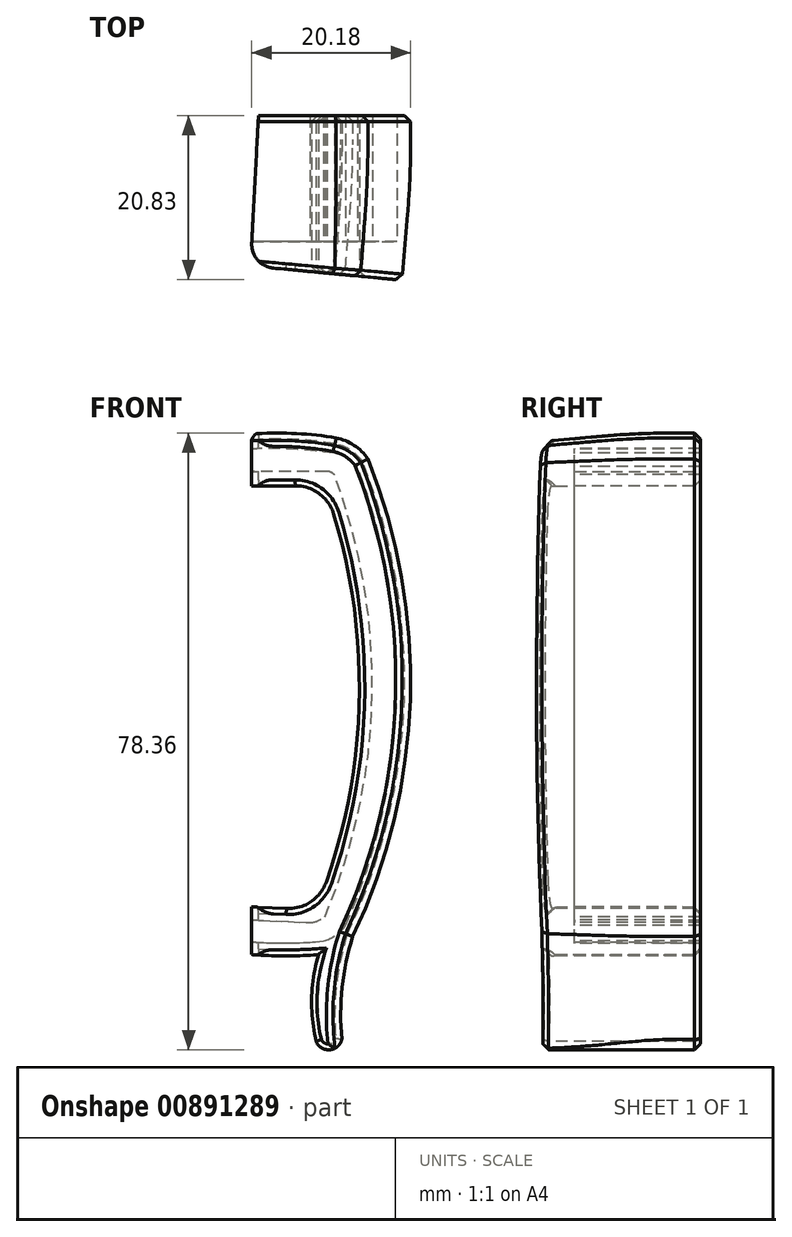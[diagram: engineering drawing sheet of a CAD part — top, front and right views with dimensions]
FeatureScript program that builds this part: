
annotation { "Feature Type Name" : "Feature", "Feature Type Description" : "" }
export const myFeature = defineFeature(function(context is Context, id is Id, definition is map)
    precondition{}
    {
        {
            var Q0;
            Q0=qCreatedBy(makeId("Front.planeOp"),FACE);
            var sketch = newSketch(context, id + "F0", { "sketchPlane" : qUnion([Q0])});
            skArc(sketch, "E0", {"start": v(-38.9, -29.21) * mm, "mid": v(-32.41, -0.21) * mm, "end": v(-37.38, 29.09) * mm});
            skArc(sketch, "E1", {"start": v(-41.54, -28.08) * mm, "mid": v(-35.53, -0.12) * mm, "end": v(-40.34, 28.07) * mm});
            skArc(sketch, "E2", {"start": v(-37.38, 29.09) * mm, "mid": v(-38.7, 30.21) * mm, "end": v(-40.34, 30.8) * mm});
            skArc(sketch, "E3", {"start": v(-41.68, -31.17) * mm, "mid": v(-40.13, -30.41) * mm, "end": v(-38.9, -29.21) * mm});
            skArc(sketch, "E4", {"start": v(-43.45, -28.83) * mm, "mid": v(-42.44, -28.6) * mm, "end": v(-41.54, -28.08) * mm});
            skArc(sketch, "E5", {"start": v(-40.34, 28.07) * mm, "mid": v(-40.75, 28.38) * mm, "end": v(-41.26, 28.5) * mm});
            skLineSegment(sketch, "E6", {"start": v(-41.26, 28.5) * mm, "end": v(-50.85, 28.5) * mm});
            skArc(sketch, "E7", {"start": v(-40.34, 30.8) * mm, "mid": v(-45.58, 31.33) * mm, "end": v(-50.85, 31.34) * mm});
            skArc(sketch, "E8", {"start": v(-50.85, -31.27) * mm, "mid": v(-46.27, -31.43) * mm, "end": v(-41.68, -31.17) * mm});
            skLineSegment(sketch, "E9", {"start": v(-50.85, -28.49) * mm, "end": v(-43.45, -28.83) * mm});
            skLineSegment(sketch, "E10", {"start": v(-50.85, 31.34) * mm, "end": v(-50.85, 33.24) * mm});
            skLineSegment(sketch, "E11", {"start": v(-50.85, 28.5) * mm, "end": v(-50.85, 26.66) * mm});
            skArc(sketch, "E12", {"start": v(-40.1, 32.76) * mm, "mid": v(-45.46, 33.32) * mm, "end": v(-50.85, 33.24) * mm});
            skArc(sketch, "E13", {"start": v(-36.07, 30.09) * mm, "mid": v(-37.83, 31.8) * mm, "end": v(-40.1, 32.76) * mm});
            skArc(sketch, "E14", {"start": v(-38, -30.6) * mm, "mid": v(-30.69, -0.46) * mm, "end": v(-36.07, 30.09) * mm});
            skArc(sketch, "E15", {"start": v(-50.85, -32.89) * mm, "mid": v(-46.15, -33.05) * mm, "end": v(-41.45, -32.84) * mm});
            skArc(sketch, "E16", {"start": v(-41.45, -32.84) * mm, "mid": v(-39.6, -31.9) * mm, "end": v(-38, -30.6) * mm});
            skLineSegment(sketch, "E17", {"start": v(-50.85, -31.27) * mm, "end": v(-50.85, -32.89) * mm});
            skLineSegment(sketch, "E18", {"start": v(-50.85, -28.49) * mm, "end": v(-50.85, -26.83) * mm});
            skLineSegment(sketch, "E19", {"start": v(-50.85, -26.83) * mm, "end": v(-43.45, -27.17) * mm});
            skArc(sketch, "E20", {"start": v(-42.57, -26.88) * mm, "mid": v(-37.16, -0.2) * mm, "end": v(-41.61, 26.66) * mm});
            skArc(sketch, "E21", {"start": v(-43.45, -27.17) * mm, "mid": v(-42.98, -27.1) * mm, "end": v(-42.57, -26.88) * mm});
            skLineSegment(sketch, "E22", {"start": v(-50.85, 26.66) * mm, "end": v(-41.61, 26.66) * mm});
            skLineSegment(sketch, "E23", {"start": v(-50.85, 31.34) * mm, "end": v(-50.85, 28.5) * mm});
            skLineSegment(sketch, "E24", {"start": v(-50.85, -28.49) * mm, "end": v(-50.85, -31.27) * mm});
            skArc(sketch, "E25", {"start": v(-38, -30.6) * mm, "mid": v(-39.34, -37.06) * mm, "end": v(-39.39, -43.66) * mm});
            skArc(sketch, "E26", {"start": v(-42.34, -32.9) * mm, "mid": v(-43.22, -38.4) * mm, "end": v(-42.65, -43.93) * mm});
            skArc(sketch, "E27", {"start": v(-42.65, -43.93) * mm, "mid": v(-40.92, -45) * mm, "end": v(-39.39, -43.66) * mm});
            skSolve(sketch);
        }
        {
            var Q0;
            Q0=makeQuery(id+"F0.imprint","IMPRINT",FACE,{"disambiguationData":[TD([[makeQuery(id+"F0.imprint","IMPRINT",EDGE,{"derivedFrom":sQuery(id+"F0.wireOp",EDGE,"E1")}),1.0]])]});
            var Q1;
            Q1=makeQuery(id+"F0.imprint","IMPRINT",FACE,{"disambiguationData":[TD([[makeQuery(id+"F0.imprint","IMPRINT",EDGE,{"derivedFrom":sQuery(id+"F0.wireOp",EDGE,"E0")}),-1.0]])]});
            var Q2;
            {var subQ1=sQuery(id+"F0.wireOp",EDGE,"E16");Q2=makeQuery(id+"F0.imprint","IMPRINT",FACE,{"disambiguationData":[TD([[makeQuery(id+"F0.imprint","IMPRINT",EDGE,{"derivedFrom":subQ1}),-1.0]])]});}
            extrude(context, id + "F1", {"entities" : qUnion([Q0, Q1, Q2]), "oppositeDirection" : true, "depth" : 20.07 * mm, "offsetDistance" : 25.4 * mm});
        }
        {
            var Q0;
            Q0=makeQuery(id+"F0.imprint","IMPRINT",FACE,{"disambiguationData":[TD([[makeQuery(id+"F0.imprint","IMPRINT",EDGE,{"derivedFrom":sQuery(id+"F0.wireOp",EDGE,"E0")}),1.0]])]});
            extrude(context, id + "F2", {"entities" : qUnion([Q0]), "oppositeDirection" : true, "depth" : 4.06 * mm, "offsetDistance" : 25.4 * mm});
        }
        {
            var Q0;
            Q0=makeQuery(id+"F2.opExtrude","SWEPT_BODY",BODY,{"disambiguationData":[OSD([sQuery(id+"F0.wireOp",EDGE,"E0"),sQuery(id+"F0.wireOp",EDGE,"E1"),sQuery(id+"F0.wireOp",EDGE,"E2"),sQuery(id+"F0.wireOp",EDGE,"E3"),sQuery(id+"F0.wireOp",EDGE,"E4"),sQuery(id+"F0.wireOp",EDGE,"E5"),sQuery(id+"F0.wireOp",EDGE,"E6"),sQuery(id+"F0.wireOp",EDGE,"E7"),sQuery(id+"F0.wireOp",EDGE,"E8"),sQuery(id+"F0.wireOp",EDGE,"E9"),sQuery(id+"F0.wireOp",EDGE,"E23"),sQuery(id+"F0.wireOp",EDGE,"E24")])]});
            var Q1;
            Q1=makeQuery(id+"F1.opExtrude","SWEPT_BODY",BODY,{"disambiguationData":[OSD([sQuery(id+"F0.wireOp",EDGE,"E1"),sQuery(id+"F0.wireOp",EDGE,"E4"),sQuery(id+"F0.wireOp",EDGE,"E5"),sQuery(id+"F0.wireOp",EDGE,"E6"),sQuery(id+"F0.wireOp",EDGE,"E9"),sQuery(id+"F0.wireOp",EDGE,"E11"),sQuery(id+"F0.wireOp",EDGE,"E18"),sQuery(id+"F0.wireOp",EDGE,"E19"),sQuery(id+"F0.wireOp",EDGE,"E20"),sQuery(id+"F0.wireOp",EDGE,"E21"),sQuery(id+"F0.wireOp",EDGE,"E22")])]});
            var Q2;
            Q2=makeQuery(id+"F1.opExtrude","SWEPT_BODY",BODY,{"disambiguationData":[OSD([sQuery(id+"F0.wireOp",EDGE,"E0"),sQuery(id+"F0.wireOp",EDGE,"E2"),sQuery(id+"F0.wireOp",EDGE,"E3"),sQuery(id+"F0.wireOp",EDGE,"E7"),sQuery(id+"F0.wireOp",EDGE,"E8"),sQuery(id+"F0.wireOp",EDGE,"E10"),sQuery(id+"F0.wireOp",EDGE,"E12"),sQuery(id+"F0.wireOp",EDGE,"E13"),sQuery(id+"F0.wireOp",EDGE,"E14"),sQuery(id+"F0.wireOp",EDGE,"E15"),sQuery(id+"F0.wireOp",EDGE,"E16"),sQuery(id+"F0.wireOp",EDGE,"E17")])]});
            booleanBodies(context, id + "F3", {"operationType" : BooleanOperationType.UNION, "tools" : qUnion([Q0, Q1, Q2])});
        }
        {
            var Q0;
            {var subQ0=sQuery(id+"F0.wireOp",EDGE,"E9");var subQ1=sQuery(id+"F0.wireOp",EDGE,"E8");var subQ2=sQuery(id+"F0.wireOp",EDGE,"E7");var subQ3=sQuery(id+"F0.wireOp",EDGE,"E6");var subQ4=sQuery(id+"F0.wireOp",EDGE,"E5");var subQ5=sQuery(id+"F0.wireOp",EDGE,"E4");var subQ6=sQuery(id+"F0.wireOp",EDGE,"E3");var subQ7=sQuery(id+"F0.wireOp",EDGE,"E2");var subQ8=sQuery(id+"F0.wireOp",EDGE,"E1");var subQ9=sQuery(id+"F0.wireOp",EDGE,"E0");Q0=makeQuery(id+"F3.opBoolean","MERGE",FACE,{"derivedFrom":[makeQuery(id+"F1.opExtrude","CAP_FACE",FACE,{"disambiguationData":[OSD([subQ9,subQ7,subQ6,subQ2,subQ1,sQuery(id+"F0.wireOp",EDGE,"E10"),sQuery(id+"F0.wireOp",EDGE,"E12"),sQuery(id+"F0.wireOp",EDGE,"E13"),sQuery(id+"F0.wireOp",EDGE,"E14"),sQuery(id+"F0.wireOp",EDGE,"E15"),sQuery(id+"F0.wireOp",EDGE,"E17"),sQuery(id+"F0.wireOp",EDGE,"E25"),sQuery(id+"F0.wireOp",EDGE,"E26"),sQuery(id+"F0.wireOp",EDGE,"E27")])],"isStart":true}),makeQuery(id+"F1.opExtrude","CAP_FACE",FACE,{"disambiguationData":[OSD([subQ8,subQ5,subQ4,subQ3,subQ0,sQuery(id+"F0.wireOp",EDGE,"E11"),sQuery(id+"F0.wireOp",EDGE,"E18"),sQuery(id+"F0.wireOp",EDGE,"E19"),sQuery(id+"F0.wireOp",EDGE,"E20"),sQuery(id+"F0.wireOp",EDGE,"E21"),sQuery(id+"F0.wireOp",EDGE,"E22")])],"isStart":true}),makeQuery(id+"F2.opExtrude","CAP_FACE",FACE,{"disambiguationData":[OSD([subQ9,subQ8,subQ7,subQ6,subQ5,subQ4,subQ3,subQ2,subQ1,subQ0,sQuery(id+"F0.wireOp",EDGE,"E23"),sQuery(id+"F0.wireOp",EDGE,"E24")])],"isStart":true})]});}
            extrude(context, id + "F4", {"entities" : qUnion([Q0]), "operationType" : NewBodyOperationType.ADD, "depth" : 2.54 * mm, "offsetDistance" : 25.4 * mm});
        }
        {
            var Q0;
            Q0=makeQuery(id+"F4.opExtrude","CAP_EDGE",EDGE,{"disambiguationData":[OSD([sQuery(id+"F0.wireOp",EDGE,"E14")])],"isStart":false});
            var Q1;
            Q1=makeQuery(id+"F4.opExtrude","CAP_EDGE",EDGE,{"disambiguationData":[OSD([sQuery(id+"F0.wireOp",EDGE,"E12")])],"isStart":false});
            var Q2;
            Q2=makeQuery(id+"F4.opExtrude","CAP_EDGE",EDGE,{"disambiguationData":[OSD([sQuery(id+"F0.wireOp",EDGE,"E13")])],"isStart":false});
            var Q3;
            Q3=makeQuery(id+"F4.opExtrude","CAP_EDGE",EDGE,{"disambiguationData":[OSD([sQuery(id+"F0.wireOp",EDGE,"E25")])],"isStart":false});
            chamfer(context, id + "F5", {"entities" : qUnion([Q0, Q1, Q2, Q3]), "chamferType" : ChamferType.OFFSET_ANGLE, "width" : 1.27 * mm, "oppositeDirection" : false, "angle" : 85 * degree, "tangentPropagation" : true});
        }
        {
            var Q0;
            {var subQ0=sQuery(id+"F0.wireOp",EDGE,"E14");Q0=makeQuery(id+"F5.opChamfer","BLEND_EDGE",EDGE,{"blendedFrom":[makeQuery(id+"F4.opExtrude","CAP_EDGE",EDGE,{"disambiguationData":[OSD([subQ0])],"isStart":false}),makeQuery(id+"F4.boolean.opBoolean","MERGE",FACE,{"derivedFrom":[makeQuery(id+"F1.opExtrude","SWEPT_FACE",FACE,{"disambiguationData":[OSD([subQ0])]}),makeQuery(id+"F4.opExtrude","SWEPT_FACE",FACE,{"disambiguationData":[OSD([subQ0])]})]})],"blendedInto":[makeQuery(id+"F4.boolean.opBoolean","MERGE",FACE,{"derivedFrom":[makeQuery(id+"F1.opExtrude","SWEPT_FACE",FACE,{"disambiguationData":[OSD([subQ0])]}),makeQuery(id+"F4.opExtrude","SWEPT_FACE",FACE,{"disambiguationData":[OSD([subQ0])]})]})]});}
            var Q1;
            {var subQ0=sQuery(id+"F0.wireOp",EDGE,"E13");Q1=makeQuery(id+"F5.opChamfer","BLEND_EDGE",EDGE,{"blendedFrom":[makeQuery(id+"F4.opExtrude","CAP_EDGE",EDGE,{"disambiguationData":[OSD([subQ0])],"isStart":false}),makeQuery(id+"F4.boolean.opBoolean","MERGE",FACE,{"derivedFrom":[makeQuery(id+"F1.opExtrude","SWEPT_FACE",FACE,{"disambiguationData":[OSD([subQ0])]}),makeQuery(id+"F4.opExtrude","SWEPT_FACE",FACE,{"disambiguationData":[OSD([subQ0])]})]})],"blendedInto":[makeQuery(id+"F4.boolean.opBoolean","MERGE",FACE,{"derivedFrom":[makeQuery(id+"F1.opExtrude","SWEPT_FACE",FACE,{"disambiguationData":[OSD([subQ0])]}),makeQuery(id+"F4.opExtrude","SWEPT_FACE",FACE,{"disambiguationData":[OSD([subQ0])]})]})]});}
            var Q2;
            {var subQ0=sQuery(id+"F0.wireOp",EDGE,"E12");Q2=makeQuery(id+"F5.opChamfer","BLEND_EDGE",EDGE,{"blendedFrom":[makeQuery(id+"F4.opExtrude","CAP_EDGE",EDGE,{"disambiguationData":[OSD([subQ0])],"isStart":false}),makeQuery(id+"F4.boolean.opBoolean","MERGE",FACE,{"derivedFrom":[makeQuery(id+"F1.opExtrude","SWEPT_FACE",FACE,{"disambiguationData":[OSD([subQ0])]}),makeQuery(id+"F4.opExtrude","SWEPT_FACE",FACE,{"disambiguationData":[OSD([subQ0])]})]})],"blendedInto":[makeQuery(id+"F4.boolean.opBoolean","MERGE",FACE,{"derivedFrom":[makeQuery(id+"F1.opExtrude","SWEPT_FACE",FACE,{"disambiguationData":[OSD([subQ0])]}),makeQuery(id+"F4.opExtrude","SWEPT_FACE",FACE,{"disambiguationData":[OSD([subQ0])]})]})]});}
            var Q3;
            {var subQ0=sQuery(id+"F0.wireOp",EDGE,"E25");Q3=makeQuery(id+"F5.opChamfer","BLEND_EDGE",EDGE,{"blendedFrom":[makeQuery(id+"F4.opExtrude","CAP_EDGE",EDGE,{"disambiguationData":[OSD([subQ0])],"isStart":false}),makeQuery(id+"F4.boolean.opBoolean","MERGE",FACE,{"derivedFrom":[makeQuery(id+"F1.opExtrude","SWEPT_FACE",FACE,{"disambiguationData":[OSD([subQ0])]}),makeQuery(id+"F4.opExtrude","SWEPT_FACE",FACE,{"disambiguationData":[OSD([subQ0])]})]})],"blendedInto":[makeQuery(id+"F4.boolean.opBoolean","MERGE",FACE,{"derivedFrom":[makeQuery(id+"F1.opExtrude","SWEPT_FACE",FACE,{"disambiguationData":[OSD([subQ0])]}),makeQuery(id+"F4.opExtrude","SWEPT_FACE",FACE,{"disambiguationData":[OSD([subQ0])]})]})]});}
            fillet(context, id + "F6", {"entities" : qUnion([Q0, Q1, Q2, Q3]), "radius" : 101.6 * mm, "tangentPropagation" : true, "allowEdgeOverflow" : false});
        }
        {
            var Q0;
            Q0=qCreatedBy(makeId("Top.planeOp"),FACE);
            cPlane(context, id + "F7", {"entities" : qUnion([Q0]), "cplaneType" : CPlaneType.OFFSET, "offset" : 33.78 * mm, "width" : 152.4 * mm, "height" : 152.4 * mm});
        }
        {
            var Q0;
            Q0=qCreatedBy(id+"F7.planeOp",FACE);
            var sketch = newSketch(context, id + "F8", { "sketchPlane" : qUnion([Q0])});
            skLineSegment(sketch, "E28", {"start": v(-26.85, -1.3) * mm, "end": v(-60.38, 1.86) * mm});
            skLineSegment(sketch, "E29", {"start": v(-26.85, -1.3) * mm, "end": v(-51.2, -11.53) * mm});
            skLineSegment(sketch, "E30", {"start": v(-51.2, -11.53) * mm, "end": v(-60.38, 1.86) * mm});
            skLineSegment(sketch, "E31", {"start": v(-50.07, 25.3) * mm, "end": v(-58.4, 26.09) * mm});
            skLineSegment(sketch, "E32", {"start": v(-58.4, 26.09) * mm, "end": v(-60.38, 1.86) * mm});
            skLineSegment(sketch, "E33", {"start": v(-50.98, 0.97) * mm, "end": v(-49.82, 22.9) * mm});
            skLineSegment(sketch, "E34", {"start": v(-49.82, 22.9) * mm, "end": v(-50.07, 25.3) * mm});
            skSolve(sketch);
        }
        {
            var Q0;
            Q0=makeQuery(id+"F8.imprint","IMPRINT",FACE,{"disambiguationData":[TD([[makeQuery(id+"F8.imprint","IMPRINT",EDGE,{"derivedFrom":sQuery(id+"F8.wireOp",EDGE,"E28")}),1.0]])]});
            var Q1;
            {var subQ2=sQuery(id+"F8.wireOp",EDGE,"ddrIeZ3n-C3nf-GXhr-pW9J-iitOHfDZmZ50");Q1=makeQuery(id+"F8.imprint","IMPRINT",FACE,{"disambiguationData":[TD([[makeQuery(id+"F8.imprint","IMPRINT",EDGE,{"derivedFrom":subQ2}),1.0]])]});}
            var Q2;
            Q2=makeQuery(id+"F8.imprint","IMPRINT",FACE,{"disambiguationData":[TD([[makeQuery(id+"F8.imprint","IMPRINT",EDGE,{"derivedFrom":sQuery(id+"F8.wireOp",EDGE,"E31")}),1.0]])]});
            extrude(context, id + "F9", {"entities" : qUnion([Q0, Q1, Q2]), "operationType" : NewBodyOperationType.REMOVE, "oppositeDirection" : true, "depth" : 254 * mm, "offsetDistance" : 25.4 * mm});
        }
        {
            var Q0;
            {var subQ0=sQuery(id+"F0.wireOp",EDGE,"E22");var subQ1=sQuery(id+"F0.wireOp",EDGE,"E20");Q0=makeQuery(id+"F4.boolean.opBoolean","MERGE",EDGE,{"derivedFrom":[makeQuery(id+"F1.opExtrude","SWEPT_EDGE",EDGE,{"disambiguationData":[OSD([subQ1,subQ0])]}),makeQuery(id+"F4.opExtrude","SWEPT_EDGE",EDGE,{"disambiguationData":[OSD([subQ1,subQ0])]})]});}
            var Q1;
            {var subQ0=sQuery(id+"F0.wireOp",EDGE,"E21");var subQ1=sQuery(id+"F0.wireOp",EDGE,"E20");Q1=makeQuery(id+"F4.boolean.opBoolean","MERGE",EDGE,{"derivedFrom":[makeQuery(id+"F1.opExtrude","SWEPT_EDGE",EDGE,{"disambiguationData":[OSD([subQ1,subQ0])]}),makeQuery(id+"F4.opExtrude","SWEPT_EDGE",EDGE,{"disambiguationData":[OSD([subQ1,subQ0])]})]});}
            fillet(context, id + "F10", {"entities" : qUnion([Q0, Q1]), "radius" : 5.08 * mm, "tangentPropagation" : true, "allowEdgeOverflow" : false});
        }
        {
            var Q0;
            Q0=makeQuery(id+"F9.boolean.opBoolean","INTERSECT",EDGE,{"derivedFrom":[makeQuery(id+"F5.opChamfer","BLEND_FACE",FACE,{"disambiguationData":[OSD([sQuery(id+"F0.wireOp",EDGE,"E14")])]}),makeQuery(id+"F9.opExtrude","SWEPT_FACE",FACE,{"disambiguationData":[OSD([sQuery(id+"F8.wireOp",EDGE,"E28")])]})]});
            var Q1;
            Q1=makeQuery(id+"F9.boolean.opBoolean","INTERSECT",EDGE,{"derivedFrom":[makeQuery(id+"F5.opChamfer","BLEND_FACE",FACE,{"disambiguationData":[OSD([sQuery(id+"F0.wireOp",EDGE,"E13")])]}),makeQuery(id+"F9.opExtrude","SWEPT_FACE",FACE,{"disambiguationData":[OSD([sQuery(id+"F8.wireOp",EDGE,"E28")])]})]});
            var Q2;
            Q2=makeQuery(id+"F9.boolean.opBoolean","INTERSECT",EDGE,{"derivedFrom":[makeQuery(id+"F5.opChamfer","BLEND_FACE",FACE,{"disambiguationData":[OSD([sQuery(id+"F0.wireOp",EDGE,"E12")])]}),makeQuery(id+"F9.opExtrude","SWEPT_FACE",FACE,{"disambiguationData":[OSD([sQuery(id+"F8.wireOp",EDGE,"E28")])]})]});
            var Q3;
            Q3=makeQuery(id+"F9.boolean.opBoolean","INTERSECT",EDGE,{"derivedFrom":[makeQuery(id+"F5.opChamfer","BLEND_FACE",FACE,{"disambiguationData":[OSD([sQuery(id+"F0.wireOp",EDGE,"E25")])]}),makeQuery(id+"F9.opExtrude","SWEPT_FACE",FACE,{"disambiguationData":[OSD([sQuery(id+"F8.wireOp",EDGE,"E28")])]})]});
            var Q4;
            {var subQ0=sQuery(id+"F0.wireOp",EDGE,"E26");Q4=makeQuery(id+"F9.boolean.opBoolean","INTERSECT",EDGE,{"derivedFrom":[makeQuery(id+"F4.boolean.opBoolean","MERGE",FACE,{"derivedFrom":[makeQuery(id+"F1.opExtrude","SWEPT_FACE",FACE,{"disambiguationData":[OSD([subQ0])]}),makeQuery(id+"F4.opExtrude","SWEPT_FACE",FACE,{"disambiguationData":[OSD([subQ0])]})]}),makeQuery(id+"F9.opExtrude","SWEPT_FACE",FACE,{"disambiguationData":[OSD([sQuery(id+"F8.wireOp",EDGE,"E28")])]})]});}
            var Q5;
            {var subQ0=sQuery(id+"F0.wireOp",EDGE,"E27");Q5=makeQuery(id+"F9.boolean.opBoolean","INTERSECT",EDGE,{"derivedFrom":[makeQuery(id+"F4.boolean.opBoolean","MERGE",FACE,{"derivedFrom":[makeQuery(id+"F1.opExtrude","SWEPT_FACE",FACE,{"disambiguationData":[OSD([subQ0])]}),makeQuery(id+"F4.opExtrude","SWEPT_FACE",FACE,{"disambiguationData":[OSD([subQ0])]})]}),makeQuery(id+"F9.opExtrude","SWEPT_FACE",FACE,{"disambiguationData":[OSD([sQuery(id+"F8.wireOp",EDGE,"E28")])]})]});}
            var Q6;
            {var subQ0=sQuery(id+"F0.wireOp",EDGE,"E15");Q6=makeQuery(id+"F9.boolean.opBoolean","INTERSECT",EDGE,{"derivedFrom":[makeQuery(id+"F4.boolean.opBoolean","MERGE",FACE,{"derivedFrom":[makeQuery(id+"F1.opExtrude","SWEPT_FACE",FACE,{"disambiguationData":[OSD([subQ0])]}),makeQuery(id+"F4.opExtrude","SWEPT_FACE",FACE,{"disambiguationData":[OSD([subQ0])]})]}),makeQuery(id+"F9.opExtrude","SWEPT_FACE",FACE,{"disambiguationData":[OSD([sQuery(id+"F8.wireOp",EDGE,"E28")])]})]});}
            var Q7;
            {var subQ0=sQuery(id+"F0.wireOp",EDGE,"E21");var subQ1=sQuery(id+"F0.wireOp",EDGE,"E20");Q7=makeQuery(id+"F10.opFillet","BLEND_EDGE",EDGE,{"blendedFrom":[makeQuery(id+"F4.boolean.opBoolean","MERGE",EDGE,{"derivedFrom":[makeQuery(id+"F1.opExtrude","SWEPT_EDGE",EDGE,{"disambiguationData":[OSD([subQ1,subQ0])]}),makeQuery(id+"F4.opExtrude","SWEPT_EDGE",EDGE,{"disambiguationData":[OSD([subQ1,subQ0])]})]}),makeQuery(id+"F9.boolean.opBoolean","COPY",FACE,{"derivedFrom":makeQuery(id+"F9.opExtrude","SWEPT_FACE",FACE,{"disambiguationData":[OSD([sQuery(id+"F8.wireOp",EDGE,"E28")])]})})],"blendedInto":[makeQuery(id+"F9.boolean.opBoolean","COPY",FACE,{"derivedFrom":makeQuery(id+"F9.opExtrude","SWEPT_FACE",FACE,{"disambiguationData":[OSD([sQuery(id+"F8.wireOp",EDGE,"E28")])]})})]});}
            var Q8;
            {var subQ0=sQuery(id+"F0.wireOp",EDGE,"E20");Q8=makeQuery(id+"F9.boolean.opBoolean","INTERSECT",EDGE,{"derivedFrom":[makeQuery(id+"F4.boolean.opBoolean","MERGE",FACE,{"derivedFrom":[makeQuery(id+"F1.opExtrude","SWEPT_FACE",FACE,{"disambiguationData":[OSD([subQ0])]}),makeQuery(id+"F4.opExtrude","SWEPT_FACE",FACE,{"disambiguationData":[OSD([subQ0])]})]}),makeQuery(id+"F9.opExtrude","SWEPT_FACE",FACE,{"disambiguationData":[OSD([sQuery(id+"F8.wireOp",EDGE,"E28")])]})]});}
            var Q9;
            {var subQ0=sQuery(id+"F0.wireOp",EDGE,"E19");Q9=makeQuery(id+"F9.boolean.opBoolean","INTERSECT",EDGE,{"derivedFrom":[makeQuery(id+"F4.boolean.opBoolean","MERGE",FACE,{"derivedFrom":[makeQuery(id+"F1.opExtrude","SWEPT_FACE",FACE,{"disambiguationData":[OSD([subQ0])]}),makeQuery(id+"F4.opExtrude","SWEPT_FACE",FACE,{"disambiguationData":[OSD([subQ0])]})]}),makeQuery(id+"F9.opExtrude","SWEPT_FACE",FACE,{"disambiguationData":[OSD([sQuery(id+"F8.wireOp",EDGE,"E28")])]})]});}
            var Q10;
            {var subQ0=sQuery(id+"F0.wireOp",EDGE,"E22");var subQ1=sQuery(id+"F0.wireOp",EDGE,"E20");Q10=makeQuery(id+"F10.opFillet","BLEND_EDGE",EDGE,{"blendedFrom":[makeQuery(id+"F4.boolean.opBoolean","MERGE",EDGE,{"derivedFrom":[makeQuery(id+"F1.opExtrude","SWEPT_EDGE",EDGE,{"disambiguationData":[OSD([subQ1,subQ0])]}),makeQuery(id+"F4.opExtrude","SWEPT_EDGE",EDGE,{"disambiguationData":[OSD([subQ1,subQ0])]})]}),makeQuery(id+"F9.boolean.opBoolean","COPY",FACE,{"derivedFrom":makeQuery(id+"F9.opExtrude","SWEPT_FACE",FACE,{"disambiguationData":[OSD([sQuery(id+"F8.wireOp",EDGE,"E28")])]})})],"blendedInto":[makeQuery(id+"F9.boolean.opBoolean","COPY",FACE,{"derivedFrom":makeQuery(id+"F9.opExtrude","SWEPT_FACE",FACE,{"disambiguationData":[OSD([sQuery(id+"F8.wireOp",EDGE,"E28")])]})})]});}
            var Q11;
            {var subQ0=sQuery(id+"F0.wireOp",EDGE,"E22");Q11=makeQuery(id+"F9.boolean.opBoolean","INTERSECT",EDGE,{"derivedFrom":[makeQuery(id+"F4.boolean.opBoolean","MERGE",FACE,{"derivedFrom":[makeQuery(id+"F1.opExtrude","SWEPT_FACE",FACE,{"disambiguationData":[OSD([subQ0])]}),makeQuery(id+"F4.opExtrude","SWEPT_FACE",FACE,{"disambiguationData":[OSD([subQ0])]})]}),makeQuery(id+"F9.opExtrude","SWEPT_FACE",FACE,{"disambiguationData":[OSD([sQuery(id+"F8.wireOp",EDGE,"E28")])]})]});}
            var Q12;
            Q12=makeQuery(id+"F1.opExtrude","CAP_EDGE",EDGE,{"disambiguationData":[OSD([sQuery(id+"F0.wireOp",EDGE,"E20")])],"isStart":false});
            var Q13;
            Q13=makeQuery(id+"F1.opExtrude","CAP_EDGE",EDGE,{"disambiguationData":[OSD([sQuery(id+"F0.wireOp",EDGE,"E14")])],"isStart":false});
            var Q14;
            Q14=makeQuery(id+"F1.opExtrude","CAP_EDGE",EDGE,{"disambiguationData":[OSD([sQuery(id+"F0.wireOp",EDGE,"E13")])],"isStart":false});
            var Q15;
            Q15=makeQuery(id+"F1.opExtrude","CAP_EDGE",EDGE,{"disambiguationData":[OSD([sQuery(id+"F0.wireOp",EDGE,"E12")])],"isStart":false});
            var Q16;
            Q16=makeQuery(id+"F1.opExtrude","CAP_EDGE",EDGE,{"disambiguationData":[OSD([sQuery(id+"F0.wireOp",EDGE,"E25")])],"isStart":false});
            var Q17;
            Q17=makeQuery(id+"F1.opExtrude","CAP_EDGE",EDGE,{"disambiguationData":[OSD([sQuery(id+"F0.wireOp",EDGE,"E26")])],"isStart":false});
            var Q18;
            Q18=makeQuery(id+"F1.opExtrude","CAP_EDGE",EDGE,{"disambiguationData":[OSD([sQuery(id+"F0.wireOp",EDGE,"E27")])],"isStart":false});
            var Q19;
            Q19=makeQuery(id+"F1.opExtrude","CAP_EDGE",EDGE,{"disambiguationData":[OSD([sQuery(id+"F0.wireOp",EDGE,"E15")])],"isStart":false});
            chamfer(context, id + "F11", {"entities" : qUnion([Q0, Q1, Q2, Q3, Q4, Q5, Q6, Q7, Q8, Q9, Q10, Q11, Q12, Q13, Q14, Q15, Q16, Q17, Q18, Q19]), "width" : 0.76 * mm, "tangentPropagation" : true});
        }
        {
            var Q0;
            {var subQ0=sQuery(id+"F0.wireOp",EDGE,"E23");var subQ1=sQuery(id+"F0.wireOp",EDGE,"E11");var subQ2=sQuery(id+"F0.wireOp",EDGE,"E10");Q0=makeQuery(id+"F9.boolean.opBoolean","INTERSECT",EDGE,{"derivedFrom":[makeQuery(id+"F4.boolean.opBoolean","MERGE",FACE,{"derivedFrom":[makeQuery(id+"F3.opBoolean","MERGE",FACE,{"derivedFrom":[makeQuery(id+"F1.opExtrude","SWEPT_FACE",FACE,{"disambiguationData":[OSD([subQ2])]}),makeQuery(id+"F1.opExtrude","SWEPT_FACE",FACE,{"disambiguationData":[OSD([subQ1])]}),makeQuery(id+"F2.opExtrude","SWEPT_FACE",FACE,{"disambiguationData":[OSD([subQ0])]})]}),makeQuery(id+"F4.opExtrude","SWEPT_FACE",FACE,{"disambiguationData":[OSD([subQ2,subQ1,subQ0])]})]}),makeQuery(id+"F9.opExtrude","SWEPT_FACE",FACE,{"disambiguationData":[OSD([sQuery(id+"F8.wireOp",EDGE,"E28")])]})]});}
            var Q1;
            {var subQ0=sQuery(id+"F0.wireOp",EDGE,"E24");var subQ1=sQuery(id+"F0.wireOp",EDGE,"E18");var subQ2=sQuery(id+"F0.wireOp",EDGE,"E17");Q1=makeQuery(id+"F9.boolean.opBoolean","INTERSECT",EDGE,{"derivedFrom":[makeQuery(id+"F4.boolean.opBoolean","MERGE",FACE,{"derivedFrom":[makeQuery(id+"F3.opBoolean","MERGE",FACE,{"derivedFrom":[makeQuery(id+"F1.opExtrude","SWEPT_FACE",FACE,{"disambiguationData":[OSD([subQ2])]}),makeQuery(id+"F1.opExtrude","SWEPT_FACE",FACE,{"disambiguationData":[OSD([subQ1])]}),makeQuery(id+"F2.opExtrude","SWEPT_FACE",FACE,{"disambiguationData":[OSD([subQ0])]})]}),makeQuery(id+"F4.opExtrude","SWEPT_FACE",FACE,{"disambiguationData":[OSD([subQ2,subQ1,subQ0])]})]}),makeQuery(id+"F9.opExtrude","SWEPT_FACE",FACE,{"disambiguationData":[OSD([sQuery(id+"F8.wireOp",EDGE,"E28")])]})]});}
            fillet(context, id + "F12", {"entities" : qUnion([Q0, Q1]), "radius" : 3.05 * mm, "tangentPropagation" : true, "allowEdgeOverflow" : false});
        }
    });
